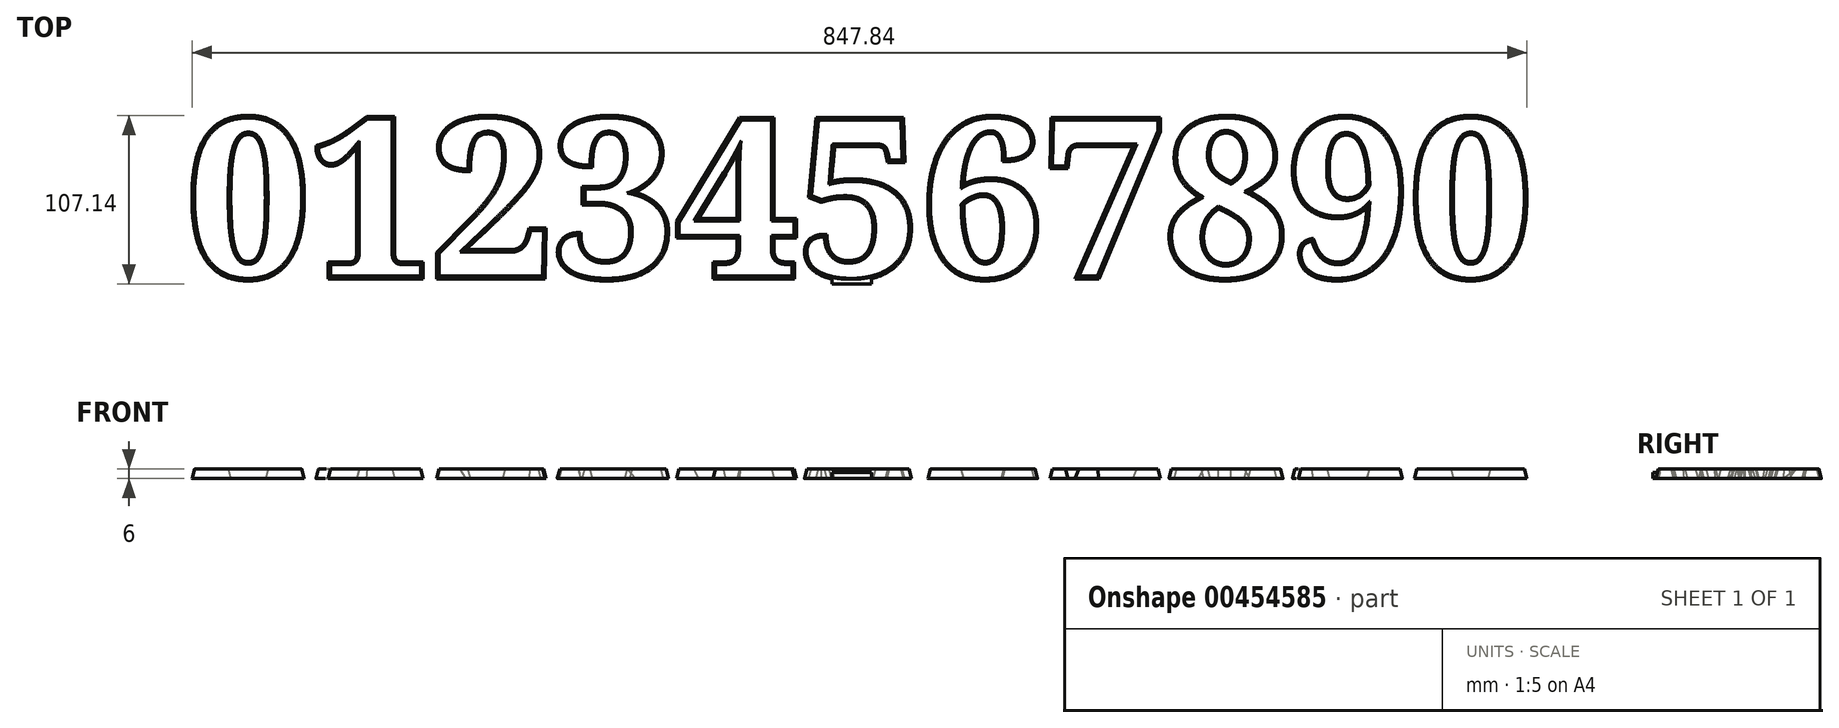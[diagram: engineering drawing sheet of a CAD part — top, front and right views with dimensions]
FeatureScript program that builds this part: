
annotation { "Feature Type Name" : "Feature", "Feature Type Description" : "" }
export const myFeature = defineFeature(function(context is Context, id is Id, definition is map)
    precondition{}
    {
        {
            var Q0;
            Q0=qCreatedBy(makeId("Top.planeOp"),FACE);
            var sketch = newSketch(context, id + "F0", { "sketchPlane" : qUnion([Q0])});
            skText(sketch, "E0", { "text": "01234567890", "fontName": "NotoSerif-Bold.ttf"});
            const initialGuessF0  = {"E0": [-0.42919, -0.05024, 1, 0, 0.1]};
            skSetInitialGuess(sketch, initialGuessF0);
            skSolve(sketch);
        }
        {
            var Q0;
            Q0=qSketchRegion(id+"F0",true);
            extrude(context, id + "F1", {"entities" : qUnion([Q0]), "oppositeDirection" : true, "depth" : 6 * mm, "hasDraft" : true, "draftAngle" : 15 * degree});
        }
        {
            var Q0;
            Q0=makeQuery(id+"F1.opExtrude","CAP_FACE",FACE,{"disambiguationData":[OSD([sQuery(id+"F0.wireOp",EDGE,"E0.sketch_text.stroke-184"),sQuery(id+"F0.wireOp",EDGE,"E0.sketch_text.stroke-185"),sQuery(id+"F0.wireOp",EDGE,"E0.sketch_text.stroke-186"),sQuery(id+"F0.wireOp",EDGE,"E0.sketch_text.stroke-187"),sQuery(id+"F0.wireOp",EDGE,"E0.sketch_text.stroke-188"),sQuery(id+"F0.wireOp",EDGE,"E0.sketch_text.stroke-189"),sQuery(id+"F0.wireOp",EDGE,"E0.sketch_text.stroke-190"),sQuery(id+"F0.wireOp",EDGE,"E0.sketch_text.stroke-191"),sQuery(id+"F0.wireOp",EDGE,"E0.sketch_text.stroke-192"),sQuery(id+"F0.wireOp",EDGE,"E0.sketch_text.stroke-193"),sQuery(id+"F0.wireOp",EDGE,"E0.sketch_text.stroke-194"),sQuery(id+"F0.wireOp",EDGE,"E0.sketch_text.stroke-195"),sQuery(id+"F0.wireOp",EDGE,"E0.sketch_text.stroke-196"),sQuery(id+"F0.wireOp",EDGE,"E0.sketch_text.stroke-197"),sQuery(id+"F0.wireOp",EDGE,"E0.sketch_text.stroke-198"),sQuery(id+"F0.wireOp",EDGE,"E0.sketch_text.stroke-199"),sQuery(id+"F0.wireOp",EDGE,"E0.sketch_text.stroke-200"),sQuery(id+"F0.wireOp",EDGE,"E0.sketch_text.stroke-201"),sQuery(id+"F0.wireOp",EDGE,"E0.sketch_text.stroke-202"),sQuery(id+"F0.wireOp",EDGE,"E0.sketch_text.stroke-203"),sQuery(id+"F0.wireOp",EDGE,"E0.sketch_text.stroke-204"),sQuery(id+"F0.wireOp",EDGE,"E0.sketch_text.stroke-205"),sQuery(id+"F0.wireOp",EDGE,"E0.sketch_text.stroke-206"),sQuery(id+"F0.wireOp",EDGE,"E0.sketch_text.stroke-207"),sQuery(id+"F0.wireOp",EDGE,"E0.sketch_text.stroke-208"),sQuery(id+"F0.wireOp",EDGE,"E0.sketch_text.stroke-209"),sQuery(id+"F0.wireOp",EDGE,"E0.sketch_text.stroke-210"),sQuery(id+"F0.wireOp",EDGE,"E0.sketch_text.stroke-211"),sQuery(id+"F0.wireOp",EDGE,"E0.sketch_text.stroke-212"),sQuery(id+"F0.wireOp",EDGE,"E0.sketch_text.stroke-213"),sQuery(id+"F0.wireOp",EDGE,"E0.sketch_text.stroke-214"),sQuery(id+"F0.wireOp",EDGE,"E0.sketch_text.stroke-215"),sQuery(id+"F0.wireOp",EDGE,"E0.sketch_text.stroke-216"),sQuery(id+"F0.wireOp",EDGE,"E0.sketch_text.stroke-217"),sQuery(id+"F0.wireOp",EDGE,"E0.sketch_text.stroke-218"),sQuery(id+"F0.wireOp",EDGE,"E0.sketch_text.stroke-219"),sQuery(id+"F0.wireOp",EDGE,"E0.sketch_text.stroke-220"),sQuery(id+"F0.wireOp",EDGE,"E0.sketch_text.stroke-221"),sQuery(id+"F0.wireOp",EDGE,"E0.sketch_text.stroke-222"),sQuery(id+"F0.wireOp",EDGE,"E0.sketch_text.stroke-223"),sQuery(id+"F0.wireOp",EDGE,"E0.sketch_text.stroke-224"),sQuery(id+"F0.wireOp",EDGE,"E0.sketch_text.stroke-225"),sQuery(id+"F0.wireOp",EDGE,"E0.sketch_text.stroke-226"),sQuery(id+"F0.wireOp",EDGE,"E0.sketch_text.stroke-227"),sQuery(id+"F0.wireOp",EDGE,"E0.sketch_text.stroke-228"),sQuery(id+"F0.wireOp",EDGE,"E0.sketch_text.stroke-229"),sQuery(id+"F0.wireOp",EDGE,"E0.sketch_text.stroke-230"),sQuery(id+"F0.wireOp",EDGE,"E0.sketch_text.stroke-231")])],"isStart":true});
            var sketch = newSketch(context, id + "F2", { "sketchPlane" : qUnion([Q0])});
            skLineSegment(sketch, "E1.bottom", {"start": v(-44.33, -9.28) * mm, "end": v(-19.33, -9.28) * mm});
            skLineSegment(sketch, "E1.top", {"start": v(-44.33, -15.28) * mm, "end": v(-19.33, -15.28) * mm});
            skLineSegment(sketch, "E1.left", {"start": v(-44.33, -9.28) * mm, "end": v(-44.33, -15.28) * mm});
            skLineSegment(sketch, "E1.right", {"start": v(-19.33, -9.28) * mm, "end": v(-19.33, -15.28) * mm});
            skSolve(sketch);
        }
        {
            var Q0;
            Q0=makeQuery(id+"F2.imprint","IMPRINT",FACE,{"disambiguationData":[TD([[makeQuery(id+"F2.imprint","IMPRINT",EDGE,{"derivedFrom":sQuery(id+"F2.wireOp",EDGE,"E1.bottom")}),-1.0]])]});
            extrude(context, id + "F3", {"entities" : qUnion([Q0]), "depth" : 4 * mm});
        }
        {
            var Q0;
            Q0=makeQuery(id+"F3.opExtrude","CAP_EDGE",EDGE,{"disambiguationData":[OSD([sQuery(id+"F2.wireOp",EDGE,"E1.top")])],"isStart":false});
            cPoint(context, id + "F4", {"entities" : qUnion([Q0]), "parameter" : 0.5});
        }
        {
            var Q0;
            Q0=makeQuery(id+"F3.opExtrude","SWEPT_BODY",BODY,{"disambiguationData":[OSD([sQuery(id+"F2.wireOp",EDGE,"E1.bottom"),sQuery(id+"F2.wireOp",EDGE,"E1.top"),sQuery(id+"F2.wireOp",EDGE,"E1.left"),sQuery(id+"F2.wireOp",EDGE,"E1.right")])]});
            var Q1;
            Q1=makeQuery(id+"F1.opExtrude","CAP_VERTEX",VERTEX,{"disambiguationData":[OSD([sQuery(id+"F0.wireOp",EDGE,"E0.sketch_text.stroke-221"),sQuery(id+"F0.wireOp",EDGE,"E0.sketch_text.stroke-222")])],"isStart":false});
            var Q2;
            Q2 = qCreatedBy(id + "F4" ,VERTEX);
            transform(context, id + "F5", {"entities" : qUnion([Q0]), "transformType" : TransformType.TRANSLATION_DISTANCE, "transformDirection" : qUnion([Q1, Q2]), "distance" : 38.4 * mm, "oppositeDirection" : true, "makeCopy" : false});
        }
        {
            var Q0;
            Q0=makeQuery(id+"F3.opExtrude","CAP_EDGE",EDGE,{"disambiguationData":[OSD([sQuery(id+"F2.wireOp",EDGE,"E1.top")])],"isStart":true});
            cPoint(context, id + "F6", {"entities" : qUnion([Q0]), "parameter" : 0.5});
        }
        {
            var Q0;
            Q0=makeQuery(id+"F3.opExtrude","CAP_EDGE",EDGE,{"disambiguationData":[OSD([sQuery(id+"F2.wireOp",EDGE,"E1.top")])],"isStart":true});
            cPoint(context, id + "F7", {"entities" : qUnion([Q0]), "parameter" : 0.5});
        }
        {
            var Q0;
            Q0=makeQuery(id+"F1.opExtrude","CAP_EDGE",EDGE,{"disambiguationData":[OSD([sQuery(id+"F0.wireOp",EDGE,"E0.sketch_text.stroke-222")])],"isStart":false});
            cPoint(context, id + "F8", {"entities" : qUnion([Q0]), "parameter" : 0.5});
        }
        {
            var Q0;
            Q0=makeQuery(id+"F3.opExtrude","SWEPT_BODY",BODY,{"disambiguationData":[OSD([sQuery(id+"F2.wireOp",EDGE,"E1.bottom"),sQuery(id+"F2.wireOp",EDGE,"E1.top"),sQuery(id+"F2.wireOp",EDGE,"E1.left"),sQuery(id+"F2.wireOp",EDGE,"E1.right")])]});
            var Q1;
            Q1 = qCreatedBy(id + "F7" ,VERTEX);
            var Q2;
            Q2 = qCreatedBy(id + "F8" ,VERTEX);
            var Q3;
            Q3 = qCreatedBy(id + "F6" ,VERTEX);
            var Q4;
            Q4=makeQuery(id+"F1.opExtrude","CAP_VERTEX",VERTEX,{"disambiguationData":[OSD([sQuery(id+"F0.wireOp",EDGE,"E0.sketch_text.stroke-221"),sQuery(id+"F0.wireOp",EDGE,"E0.sketch_text.stroke-222")])],"isStart":false});
            transform(context, id + "F9", {"entities" : qUnion([Q0]), "transformType" : TransformType.TRANSLATION_ENTITY, "oppositeDirectionEntity" : false, "transformLine" : qUnion([Q1, Q2]), "makeCopy" : false});
        }
        {
            var Q0;
            Q0=makeQuery(id+"F3.opExtrude","CAP_EDGE",EDGE,{"disambiguationData":[OSD([sQuery(id+"F2.wireOp",EDGE,"E1.top")])],"isStart":true});
            cPoint(context, id + "F10", {"entities" : qUnion([Q0]), "parameter" : 0.5});
        }
        {
            var Q0;
            Q0=makeQuery(id+"F3.opExtrude","SWEPT_BODY",BODY,{"disambiguationData":[OSD([sQuery(id+"F2.wireOp",EDGE,"E1.bottom"),sQuery(id+"F2.wireOp",EDGE,"E1.top"),sQuery(id+"F2.wireOp",EDGE,"E1.left"),sQuery(id+"F2.wireOp",EDGE,"E1.right")])]});
            var Q1;
            Q1 = qCreatedBy(id + "F10" ,VERTEX);
            var Q2;
            Q2=makeQuery(id+"F1.opExtrude","CAP_VERTEX",VERTEX,{"disambiguationData":[OSD([sQuery(id+"F0.wireOp",EDGE,"E0.sketch_text.stroke-221"),sQuery(id+"F0.wireOp",EDGE,"E0.sketch_text.stroke-222")])],"isStart":false});
            transform(context, id + "F11", {"entities" : qUnion([Q0]), "transformType" : TransformType.TRANSLATION_ENTITY, "oppositeDirectionEntity" : false, "transformLine" : qUnion([Q1, Q2]), "makeCopy" : false});
        }
        {
            var Q0;
            Q0=makeQuery(id+"F3.opExtrude","SWEPT_FACE",FACE,{"disambiguationData":[OSD([sQuery(id+"F2.wireOp",EDGE,"E1.top")])]});
            extrude(context, id + "F12", {"entities" : qUnion([Q0]), "operationType" : NewBodyOperationType.ADD, "depth" : 2 * mm});
        }
    });
